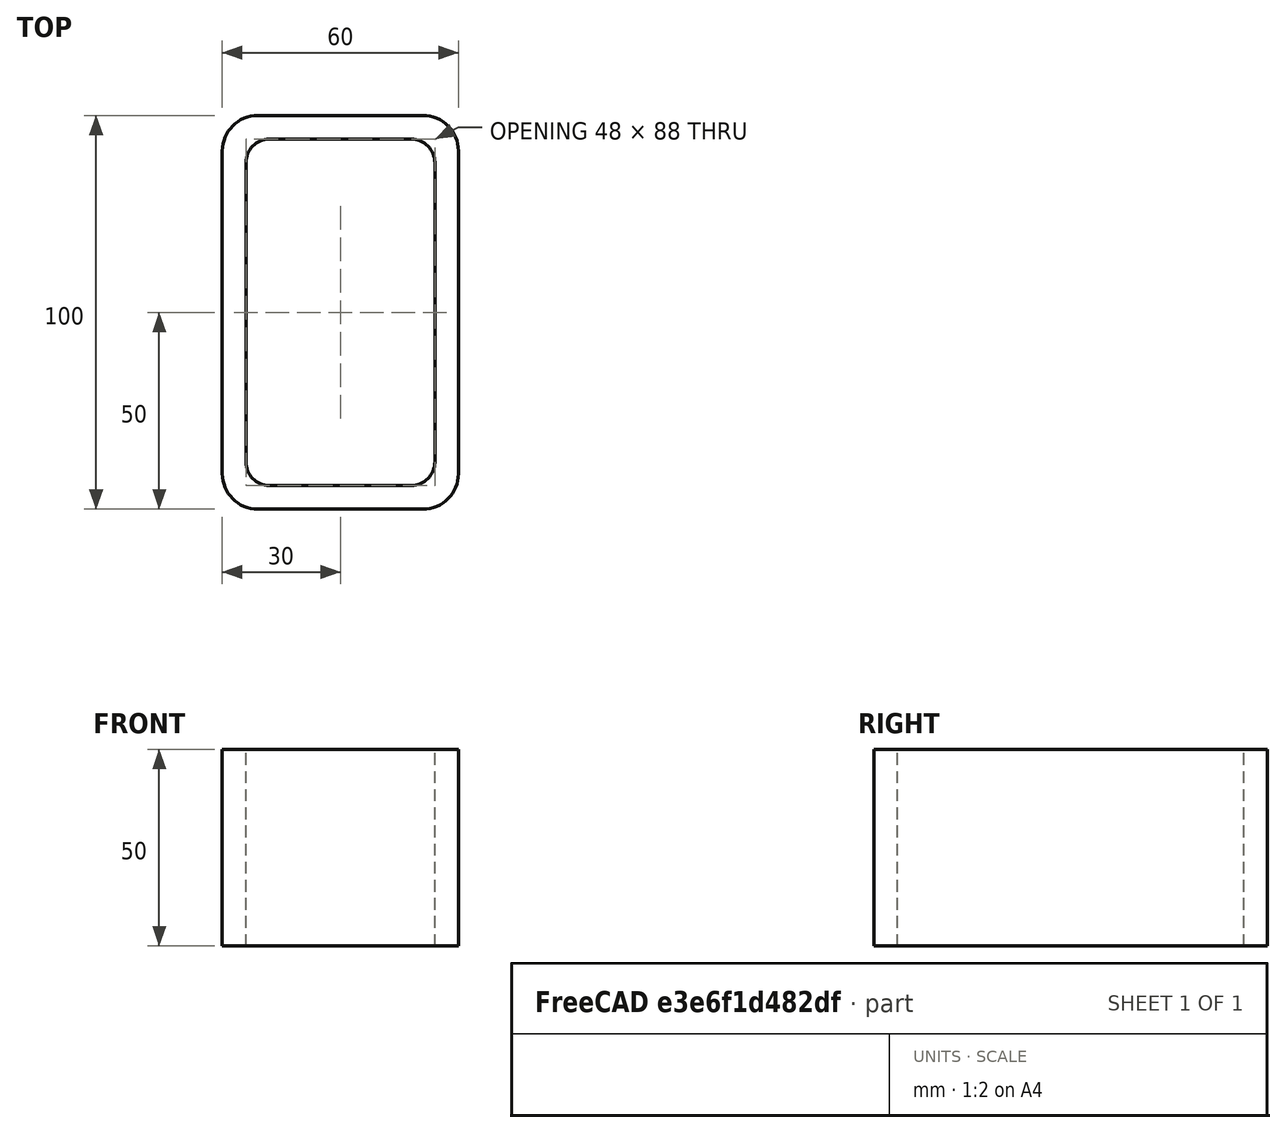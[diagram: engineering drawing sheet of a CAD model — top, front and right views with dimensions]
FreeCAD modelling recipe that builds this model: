
FCSTD DOCUMENT  (FreeCAD 0.15R4671 (Git))
Label: Rectangular hollow section 100x60x6 EN10219 S235JRH
License: All rights reserved
LicenseURL: http://en.wikipedia.org/wiki/All_rights_reserved
objects: Sketcher::SketchObject×1, Part::Extrusion×1
note: 2 computed .brp shape members not serialized (recipe doc carries the construction recipe); baked Part::Feature solids carry a one-line shape summary decoded from their .brp

FEATURE [Sketcher::SketchObject] Sketch
  sketch-geometry (16):
    g0: LineSegment StartX=-18 StartY=44 StartZ=0 EndX=18 EndY=44 EndZ=0
    g1: LineSegment StartX=24 StartY=38 StartZ=0 EndX=24 EndY=-38 EndZ=0
    g2: LineSegment StartX=18 StartY=-44 StartZ=0 EndX=-18 EndY=-44 EndZ=0
    g3: LineSegment StartX=-24 StartY=-38 StartZ=0 EndX=-24 EndY=38 EndZ=0
    g4: LineSegment StartX=-21 StartY=50 StartZ=0 EndX=21 EndY=50 EndZ=0
    g5: LineSegment StartX=30 StartY=41 StartZ=0 EndX=30 EndY=-41 EndZ=0
    g6: LineSegment StartX=21 StartY=-50 StartZ=0 EndX=-21 EndY=-50 EndZ=0
    g7: LineSegment StartX=-30 StartY=-41 StartZ=0 EndX=-30 EndY=41 EndZ=0
    g8: ArcOfCircle CenterX=-18 CenterY=38 CenterZ=0 NormalX=0 NormalY=0 NormalZ=1 Radius=6 StartAngle=1.5708 EndAngle=3.14159
    g9: ArcOfCircle CenterX=18 CenterY=38 CenterZ=0 NormalX=0 NormalY=0 NormalZ=1 Radius=6 StartAngle=0 EndAngle=1.5708
    g10: ArcOfCircle CenterX=18 CenterY=-38 CenterZ=0 NormalX=0 NormalY=0 NormalZ=1 Radius=6 StartAngle=4.71239 EndAngle=6.28319
    g11: ArcOfCircle CenterX=-18 CenterY=-38 CenterZ=0 NormalX=0 NormalY=0 NormalZ=1 Radius=6 StartAngle=3.14159 EndAngle=4.71239
    g12: ArcOfCircle CenterX=21 CenterY=41 CenterZ=0 NormalX=0 NormalY=0 NormalZ=1 Radius=9 StartAngle=0 EndAngle=1.5708
    g13: ArcOfCircle CenterX=21 CenterY=-41 CenterZ=0 NormalX=0 NormalY=0 NormalZ=1 Radius=9 StartAngle=4.71239 EndAngle=6.28319
    g14: ArcOfCircle CenterX=-21 CenterY=-41 CenterZ=0 NormalX=0 NormalY=0 NormalZ=1 Radius=9 StartAngle=3.14159 EndAngle=4.71239
    g15: ArcOfCircle CenterX=-21 CenterY=41 CenterZ=0 NormalX=0 NormalY=0 NormalZ=1 Radius=9 StartAngle=1.5708 EndAngle=3.14159
  constraints (36):
    c: Horizontal(g2)
    c: Vertical(g3)
    c: Horizontal(g6)
    c: Vertical(g7)
    c: Tangent(g3,g8) = 1.5708
    c: Tangent(g0,g8) = 1.5708
    c: Tangent(g0,g9) = 1.5708
    c: Tangent(g1,g9) = 1.5708
    c: Tangent(g1,g10) = 1.5708
    c: Tangent(g2,g10) = 1.5708
    c: Tangent(g2,g11) = 1.5708
    c: Tangent(g3,g11) = 1.5708
    c: Tangent(g4,g12) = 1.5708
    c: Tangent(g5,g12) = 1.5708
    c: Tangent(g5,g13) = 1.5708
    c: Tangent(g6,g13) = 1.5708
    c: Tangent(g6,g14) = 1.5708
    c: Tangent(g7,g14) = 1.5708
    c: Tangent(g7,g15) = 1.5708
    c: Tangent(g4,g15) = 1.5708
    c: Equal(g9,g8)
    c: Equal(g9,g11)
    c: Equal(g9,g10)
    c: Equal(g12,g15)
    c: Equal(g12,g14)
    c: Equal(g12,g13)
    c: Symmetric(g4,g6,g-1)
    c: Symmetric(g7,g5,g-2)
    c: DistanceY(g4,g6) = -100
    c: DistanceX(g7,g5) = 60
    c: Symmetric(g3,g1,g-2)
    c: Symmetric(g0,g2,g-1)
    c: DistanceY(g0,g4) = 6
    c: DistanceX(g5,g1) = -6
    c: Radius(g9) = 6
    c: Radius(g12) = 9
FEATURE [Part::Extrusion] Extrude  label="Rectangular hollow section 100x60x6 EN10219 S235JRH"
  Base = -> Sketch
  Dir = (0,0,50)
  Solid = true
